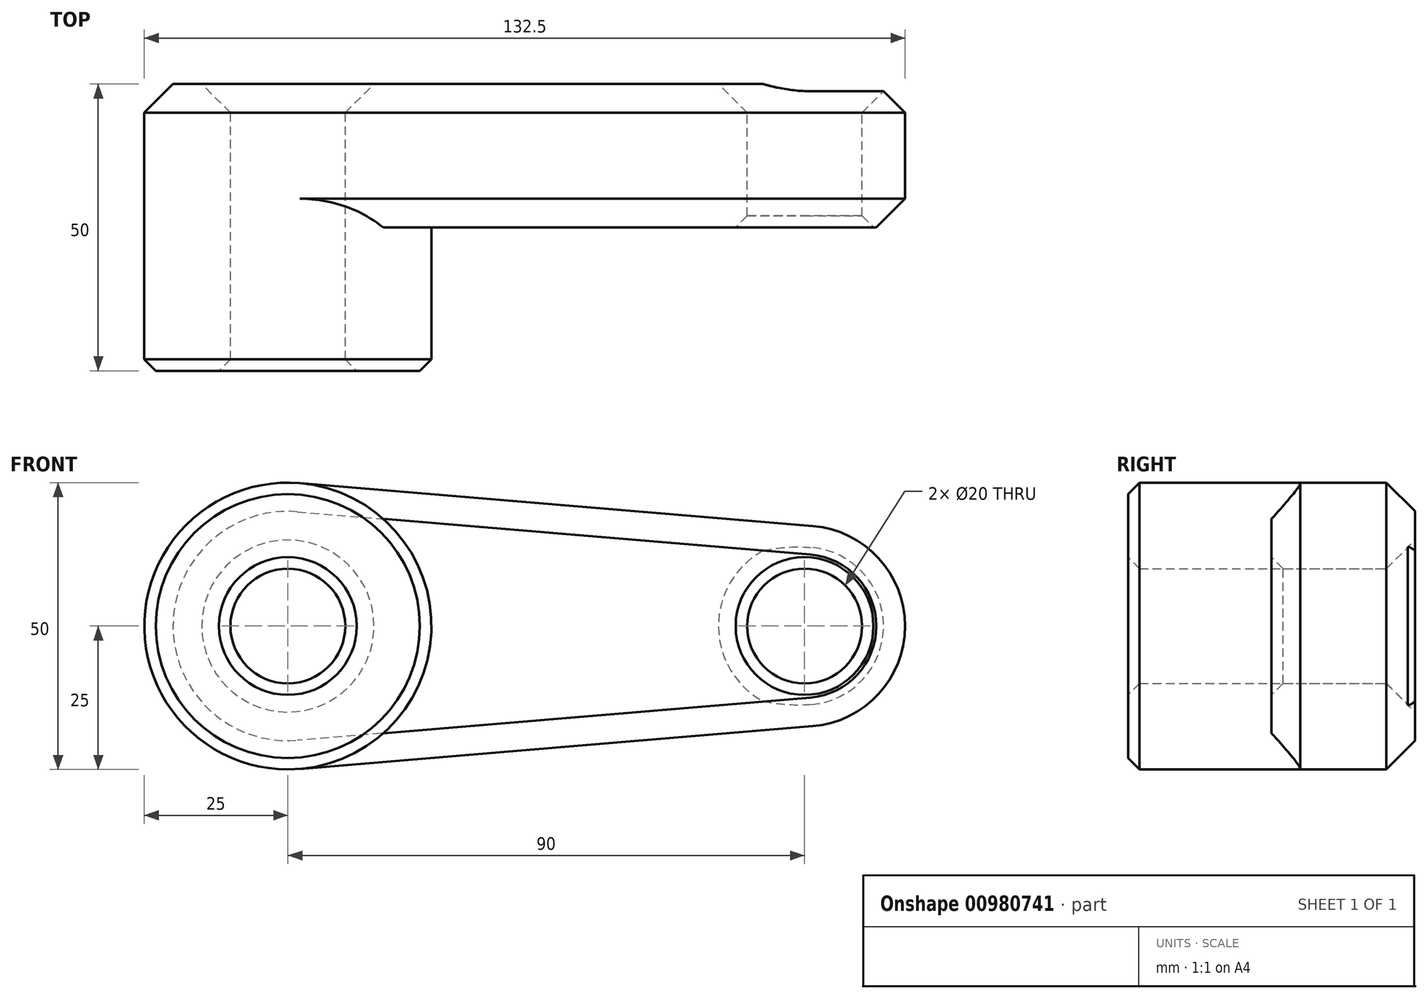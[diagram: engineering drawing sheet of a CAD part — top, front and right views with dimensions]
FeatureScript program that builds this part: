
annotation { "Feature Type Name" : "Feature", "Feature Type Description" : "" }
export const myFeature = defineFeature(function(context is Context, id is Id, definition is map)
    precondition{}
    {
        {
            var Q0;
            Q0=qCreatedBy(makeId("Front.planeOp"),FACE);
            var sketch = newSketch(context, id + "F0", { "sketchPlane" : qUnion([Q0])});
            skCircle(sketch, "E0", {"center": v(0, 0) * mm, "radius": 25 * mm});
            skCircle(sketch, "E1", {"center": v(90, 0) * mm, "radius": 17.5 * mm});
            skLineSegment(sketch, "E2", {"start": v(2.08, 24.91) * mm, "end": v(91.46, 17.44) * mm});
            skLineSegment(sketch, "E3", {"start": v(2.08, -24.91) * mm, "end": v(91.46, -17.44) * mm});
            skCircle(sketch, "E4", {"center": v(0, 0) * mm, "radius": 10 * mm});
            skCircle(sketch, "E5", {"center": v(90, 0) * mm, "radius": 10 * mm});
            skSolve(sketch);
        }
        {
            var Q0;
            Q0 = qSketchRegion(id + "F0", true);
            extrude(context, id + "F1", {"entities" : qUnion([Q0]), "depth" : 25 * mm, "offsetDistance" : 25 * mm});
        }
        {
            var Q0;
            Q0=makeQuery(id+"F0.imprint","IMPRINT",FACE,{"disambiguationData":[TD([[makeQuery(id+"F0.imprint","IMPRINT",EDGE,{"derivedFrom":sQuery(id+"F0.wireOp",EDGE,"E4")}),-1.0]])]});
            extrude(context, id + "F2", {"entities" : qUnion([Q0]), "operationType" : NewBodyOperationType.ADD, "depth" : 50 * mm, "offsetDistance" : 25 * mm});
        }
        {
            var Q0;
            Q0=makeQuery(id+"F2.opExtrude","CAP_EDGE",EDGE,{"disambiguationData":[OSD([sQuery(id+"F0.wireOp",EDGE,"E0")])],"isStart":false});
            var Q1;
            Q1=makeQuery(id+"F2.opExtrude","CAP_EDGE",EDGE,{"disambiguationData":[OSD([sQuery(id+"F0.wireOp",EDGE,"E4")])],"isStart":false});
            var Q2;
            Q2=makeQuery(id+"F1.opExtrude","CAP_EDGE",EDGE,{"disambiguationData":[OSD([sQuery(id+"F0.wireOp",EDGE,"E5")])],"isStart":false});
            chamfer(context, id + "F3", {"entities" : qUnion([Q0, Q1, Q2]), "width" : 2 * mm, "tangentPropagation" : true});
        }
        {
            var Q0;
            Q0=makeQuery(id+"F1.opExtrude","CAP_EDGE",EDGE,{"disambiguationData":[OSD([sQuery(id+"F0.wireOp",EDGE,"E4")])],"isStart":true});
            var Q1;
            Q1=makeQuery(id+"F1.opExtrude","CAP_FACE",FACE,{"disambiguationData":[OSD([sQuery(id+"F0.wireOp",EDGE,"E0"),sQuery(id+"F0.wireOp",EDGE,"E1"),sQuery(id+"F0.wireOp",EDGE,"E2"),sQuery(id+"F0.wireOp",EDGE,"E3"),sQuery(id+"F0.wireOp",EDGE,"E4"),sQuery(id+"F0.wireOp",EDGE,"E5")])],"isStart":true});
            var Q2;
            Q2=makeQuery(id+"F1.opExtrude","CAP_EDGE",EDGE,{"disambiguationData":[OSD([sQuery(id+"F0.wireOp",EDGE,"E5")])],"isStart":true});
            chamfer(context, id + "F4", {"entities" : qUnion([Q0, Q1, Q2]), "width" : 5 * mm, "tangentPropagation" : true});
        }
        {
            var Q0;
            Q0=makeQuery(id+"F1.opExtrude","CAP_EDGE",EDGE,{"disambiguationData":[OSD([sQuery(id+"F0.wireOp",EDGE,"E2")])],"isStart":false});
            chamfer(context, id + "F5", {"entities" : qUnion([Q0]), "width" : 5 * mm, "tangentPropagation" : true});
        }
    });
